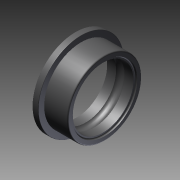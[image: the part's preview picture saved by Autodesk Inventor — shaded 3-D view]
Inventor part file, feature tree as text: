
AUTODESK INVENTOR PART (.ipt)
format: ipt  version: 2011 SP1 (Build 150282100, 282)  size: 169,984 bytes
history: native  units: mm
features: revolve x2, sketch x2
ambient origin geometry x8: Origin, YZ Plane, XZ Plane, XY Plane, X Axis, Y Axis, Z Axis, Center Point
bodies: Solid1 (feature_tree)
feature tree (4):
  revolve  "Revolution1"  Angle=360.0deg
  revolve  "Revolution2"  [1 undecoded]
  sketch  "Sketch_11"  dims[d0=360.0deg d1=360.0deg]
  sketch  "Sketch_12"
note: 1 required parameter value undecoded (feature->parameter linkage not recoverable at this tier; creation-order binding heuristic only, values carry confidence <= 0.55)
